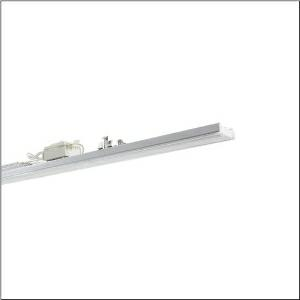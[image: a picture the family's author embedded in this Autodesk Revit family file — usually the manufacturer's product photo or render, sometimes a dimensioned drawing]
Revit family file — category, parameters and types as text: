
# Revit family: licross_r__21_recessed_ho_52te18dv4l2m_7c7f
name_source: partatom
category: Lighting Fixtures
units: mm (PartAtom-declared; Revit-internal decimal feet)

## family parameters
Cut with Voids When Loaded = No
Host = Face
Light Source = No
Part Type = Normal
Room Calculation Point = No
Round Connector Dimension = Use Diameter
Shared = No

## types (1)
- --- (1 x LED, 22480 lm, 125.6 W, 4000K)
    Apparent Load = 126 VA
    CIE Flux Codes = 75 94 99 100 100
    Color Rendering = 80
    Color Temperature = 4000K
    Default Elevation = 1800 mm
    Description = Licross® 21 Recessed HO, luminaire insert, of sheet steel, galvanised, coil coated, white, length: 2.250mm, width: 66mm, height: 67mm, LED rated luminous flux: 22.480lm, light colour: 840, control gear: DALI 2, with plug, 5-pole, with phase selection, mains connection: 220..240V, AC, 50/60Hz, rated input power: 126W, internal wiring halogen-free, primary light control with lens, of plastic, primary optical cover: cover, of PMMA, light emission: direct distribution, primary light characteristic: symmetric, protection rating (complete): IP54, insulation class (complete): insulation class I (protective earthing), certification: CE, ENEC, VDE, UKCA, protection symbol: D if used in an environment with non-conductive dust loads with corresponding accessories, impact resistance: IK06, permissible ambient temperature for indoor applications: -40..+30°C, corresponds to IFS (International Featured Standards) requirements for safety and quality in the food industry, reducing of maximum allowable ambient temperature of 5°C with ceiling mounting, LABS conformity tested according to VDMA 24364:2018-05, packaging unit: 1 piece
    Height = 58 mm
    Lamp = 1 x LED
    Lamp Light Flux = 22480 lm
    Lamp Power = 125.6 W
    Lamp count = 1
    Length = 2250 mm
    Luminous efficacy = 179 lm/W
    Manufacturer = Siteco
    ModVariant = No
    Model = 52TE18DV4L2M
    Mounting Place = Ceiling
    Mounting Type = Pendant
    Number of Poles = 1
    OnlyDefault = Yes
    Power Factor = 1
    Product Name = Licross® 21 Recessed HO
    Product group = luminaire insert | ceiling pendant
    ProductGroupID = 902
    Protection Class = Protection class I
    Protection Degree = IP 54
    RLX_Detail_Level = 1
    RLX_Emergency_Light_Flux = 0 lm
    RLX_Emergency_Type = 0
    RLX_Emergency_Type_DB = No
    RlxData = <blob elided: 29893 chars, md5=32a8a9b9>
    Socket = socket
    Standby Power = 0 W
    System Light Flux = 22480 lm
    System Power = 126 W
    Type Comments = factory setting: luminous flux: 100 % | dim-lin: 254 | 489 mA
    Type Image = l_1296930.jpg
    URL = http://relux.com
    VarID = @adj_147315
    Voltage = 0 V
    Weight = 0.00 kg
    Width = 66 mm

## geometry (parser evidence)
native form markers: Blend x4, Sweep x10
no freeform markers — native parametric forms only
